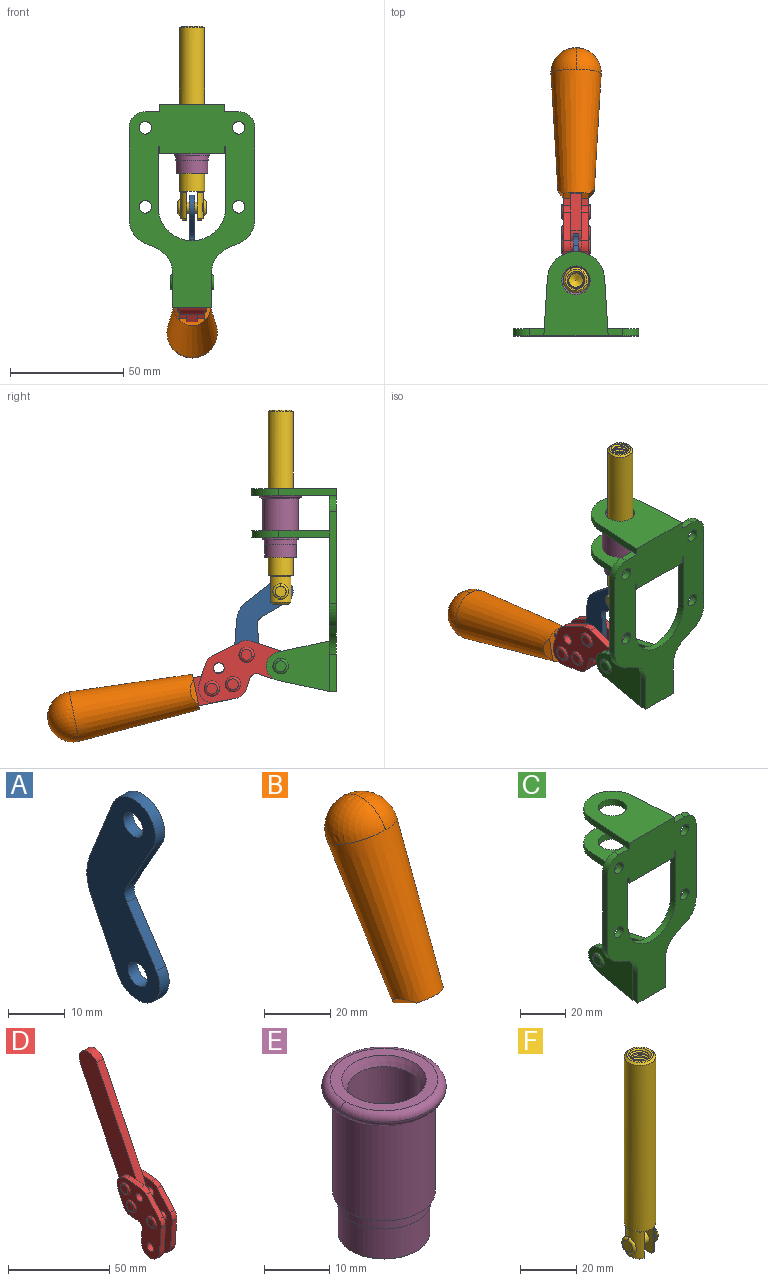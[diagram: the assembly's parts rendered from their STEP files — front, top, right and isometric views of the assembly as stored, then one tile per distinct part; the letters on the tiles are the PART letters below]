
ASSEMBLY  parts=6 mates=6
PART A: 12 faces, bbox 2.3x18.2x42.8 mm
  f0: cylinder r=2.4mm len=4.8mm, axis (1,0,0), area 34.9mm2, adj f4,f11
  f1: cylinder r=10.41mm len=8.47mm, axis (1,0,0), area 20.2mm2, adj f4,f9,f10,f11
  f2: cylinder r=3.05mm len=3.16mm, axis (1,0,0), area 7.7mm2, adj f4,f6,f7,f11
  f3: cylinder r=2.4mm len=4.8mm, axis (1,0,0), area 34.9mm2, adj f4,f11
  f4: plane 42.81x18.23mm, normal (-1,0,0), area 414.1mm2, adj f0,f1,f2,f3,f5,f6,f7,f8
  f5: cylinder r=5.54mm len=10.67mm, axis (1,0,0), area 41.8mm2, adj f4,f6,f10,f11
  f6: plane 11.66x6.53mm, normal (0,-0.87,-0.49), area 30.9mm2, adj f2,f4,f5,f11
  f7: plane 11.17x7.33mm, normal (0,-0.84,0.55), area 30.9mm2, adj f2,f4,f8,f11
  f8: cylinder r=5.54mm len=10.51mm, axis (1,0,0), area 41.8mm2, adj f4,f7,f9,f11
  f9: plane 13.67x6.67mm, normal (0,0.9,-0.44), area 35.1mm2, adj f1,f4,f8,f11
  f10: plane 14.1x5.7mm, normal (0,0.93,0.37), area 35.1mm2, adj f1,f4,f5,f11
  f11: plane 42.81x18.23mm, normal (1,0,0), area 414.1mm2, adj f0,f1,f2,f3,f5,f6,f7,f8
PART B: 11 faces, bbox 22.3x42.6x64.5 mm
  f0: sphere r=11.13mm, area 411.4mm2, adj f1,f8
  f1: cone r=11.11mm half-angle=3.3deg, axis (0,0.44,0.9), area 3251.8mm2, adj f0,f7,f8,f9,f10
  f2: cylinder r=6.16mm len=11.7mm, axis (1,0,0), area 89.5mm2, adj f3,f4,f5,f6
  f3: plane 60.23x36.75mm, normal (-1,0,0), area 763.6mm2, adj f2,f4,f6,f10
  f4: plane 51.37x25.05mm, normal (0,0.9,-0.44), area 264.2mm2, adj f2,f3,f5,f10
  f5: plane 60.23x36.75mm, normal (1,0,0), area 763.6mm2, adj f2,f4,f6,f10
  f6: plane 51.37x25.05mm, normal (0,-0.9,0.44), area 264.2mm2, adj f2,f3,f5,f10
  f7: plane 9.95x5.95mm, normal (0.71,-0.31,-0.64), area 25.8mm2, adj f1,f10
  f8: sphere r=11.13mm, area 411.4mm2, adj f0,f1
  f9: plane 9.95x5.95mm, normal (-0.71,-0.31,-0.64), area 25.8mm2, adj f1,f10
  f10: plane 14.27x11.38mm, normal (0,-0.44,-0.9), area 106.7mm2, adj f1,f3,f4,f5,f6,f7,f9
PART C: 55 faces, bbox 55.7x37.4x89.8 mm
  f0: torus R=2.41mm, axis (-1,0,0), area 15mm2, adj f11,f15,f25
  f1: torus R=2.41mm, axis (-1,0,0), area 15mm2, adj f10,f12,f22
  f2: cylinder r=2.78mm len=5.56mm, axis (0,-1,0), area 54.2mm2, adj f30,f54
  f3: cylinder r=14.99mm len=29.97mm, axis (0,-1,0), area 145.9mm2, adj f30,f49,f53,f54
  f4: cylinder r=2.78mm len=5.56mm, axis (0,-1,0), area 54.2mm2, adj f30,f54
  f5: cylinder r=2.78mm len=5.56mm, axis (0,-1,0), area 54.2mm2, adj f30,f54
  f6: cylinder r=2.78mm len=5.56mm, axis (0,-1,0), area 54.2mm2, adj f30,f54
  f7: cylinder r=6.35mm len=12.7mm, axis (0,0,1), area 123.6mm2, adj f27,f51
  f8: cylinder r=6.35mm len=12.7mm, axis (0,0,-1), area 124.7mm2, adj f21,f35
  f9: cylinder r=2.41mm len=11.18mm, axis (-1,0,0), area 169.4mm2, adj f16,f19
  f10: plane 4.83x4.83mm, normal (1,0,0), area 18.3mm2, adj f1,f12
  f11: plane 4.83x4.83mm, normal (-1,0,0), area 18.3mm2, adj f0,f15
  f12: torus R=2.41mm, axis (-1,0,0), area 15mm2, adj f1,f10,f22
  f13: cylinder r=6.35mm len=12.41mm, axis (1,0,0), area 53.4mm2, adj f18,f19,f22,f23
  f14: cylinder r=6.35mm len=12.41mm, axis (-1,0,0), area 53.4mm2, adj f16,f17,f24,f25
  f15: torus R=2.41mm, axis (-1,0,0), area 15mm2, adj f0,f11,f25
  f16: plane 27.86x22.35mm, normal (1,0,0), area 425.4mm2, adj f9,f14,f17,f24,f30
  f17: plane 22.86x4.97mm, normal (0,0.21,0.98), area 72.5mm2, adj f14,f16,f25,f30
  f18: plane 22.86x4.97mm, normal (0,0.21,0.98), area 72.5mm2, adj f13,f19,f22,f30
  f19: plane 27.86x22.35mm, normal (-1,0,0), area 425.4mm2, adj f9,f13,f18,f23,f30
  f20: cylinder r=12.7mm len=25.35mm, axis (0,0,-1), area 119.8mm2, adj f21,f34,f35,f36
  f21: plane 34.21x28.07mm, normal (0,0,-1), area 702.4mm2, adj f8,f20,f30,f34,f36
  f22: plane 27.96x22.45mm, normal (1,0,0), area 407.2mm2, adj f1,f12,f13,f18,f23,f30,f42,f43
  f23: plane 22.86x4.97mm, normal (0,0.21,-0.98), area 72.5mm2, adj f13,f19,f22,f44
  f24: plane 22.86x4.97mm, normal (0,0.21,-0.98), area 72.5mm2, adj f14,f16,f25,f44
  f25: plane 27.86x22.35mm, normal (-1,0,0), area 407.1mm2, adj f0,f14,f15,f17,f24,f30,f45,f46
  f26: plane 3.1x0.95mm, normal (0,0,-1), area 2.7mm2, adj f30,f49,f50,f54
  f27: plane 34.21x28.07mm, normal (0,0,1), area 702.4mm2, adj f7,f28,f30,f50,f52
  f28: cylinder r=12.7mm len=25.35mm, axis (0,0,1), area 118.8mm2, adj f27,f50,f51,f52
  f29: plane 3.1x0.95mm, normal (0,0,-1), area 2.7mm2, adj f30,f52,f53,f54
  f30: plane 86.54x55.63mm, normal (0,1,0), area 2362.9mm2, adj f2,f3,f4,f5,f6,f16,f17,f18
  f31: plane 40.56x3.1mm, normal (-1,0,0), area 125.7mm2, adj f30,f32,f48,f54
  f32: cylinder r=7.11mm len=7.11mm, axis (0,-1,0), area 34.6mm2, adj f30,f31,f33,f54
  f33: plane 6.67x3.1mm, normal (0,0,1), area 20.4mm2, adj f30,f32,f34,f54
  f34: plane 25.39x3.13mm, normal (-1,0.06,0), area 79.5mm2, adj f20,f21,f33,f35,f54
  f35: plane 37.31x28.45mm, normal (0,0,1), area 789.9mm2, adj f8,f20,f34,f36,f54
  f36: plane 25.39x3.13mm, normal (1,0.06,0), area 79.5mm2, adj f20,f21,f35,f37,f54
  f37: plane 6.67x3.1mm, normal (0,0,1), area 20.4mm2, adj f30,f36,f38,f54
  f38: cylinder r=7.11mm len=7.11mm, axis (0,-1,0), area 34.6mm2, adj f30,f37,f39,f54
  f39: plane 40.56x3.1mm, normal (1,0,0), area 125.7mm2, adj f30,f38,f40,f54
  f40: cylinder r=11.18mm len=10.16mm, axis (0,-1,0), area 39.5mm2, adj f30,f39,f41,f54
  f41: plane 6.09x3.1mm, normal (0.42,0,-0.91), area 20.8mm2, adj f30,f40,f42,f54
  f42: cylinder r=11.18mm len=9.41mm, axis (0,-1,0), area 37.2mm2, adj f22,f30,f41,f43,f54
  f43: plane 16.5x3.1mm, normal (1,0,0), area 51.1mm2, adj f22,f42,f44,f54
  f44: plane 17.37x3.1mm, normal (0,0,-1), area 53.8mm2, adj f23,f24,f30,f43,f45,f54
  f45: plane 16.5x3.1mm, normal (-1,0,0), area 51.1mm2, adj f25,f44,f46,f54
  f46: cylinder r=11.18mm len=9.41mm, axis (0,-1,0), area 37.2mm2, adj f25,f30,f45,f47,f54
  f47: plane 6.09x3.1mm, normal (-0.42,0,-0.91), area 20.8mm2, adj f30,f46,f48,f54
  f48: cylinder r=11.18mm len=10.16mm, axis (0,-1,0), area 39.5mm2, adj f30,f31,f47,f54
  f49: plane 26.54x3.1mm, normal (-1,0,0), area 82.3mm2, adj f3,f26,f30,f54
  f50: plane 25.39x3.1mm, normal (1,0.06,0), area 78.8mm2, adj f26,f27,f28,f51,f54
  f51: plane 37.31x28.45mm, normal (0,0,-1), area 789.9mm2, adj f7,f28,f50,f52,f54
  f52: plane 25.39x3.1mm, normal (-1,0.06,0), area 78.8mm2, adj f27,f28,f29,f51,f54
  f53: plane 26.54x3.1mm, normal (1,0,0), area 82.3mm2, adj f3,f29,f30,f54
  f54: plane 89.66x55.63mm, normal (0,-1,0), area 2678.5mm2, adj f2,f3,f4,f5,f6,f26,f29,f31
PART D: 59 faces, bbox 12.9x60.2x99.6 mm
  f0: torus R=2.39mm, axis (-1,0,0), area 14.9mm2, adj f20,f43,f51
  f1: torus R=2.39mm, axis (-1,0,0), area 14.9mm2, adj f19,f42,f51
  f2: torus R=2.39mm, axis (-1,0,0), area 14.9mm2, adj f18,f35,f51
  f3: torus R=2.39mm, axis (-1,0,0), area 14.9mm2, adj f14,f17,f23
  f4: torus R=2.39mm, axis (-1,0,0), area 14.9mm2, adj f13,f16,f23
  f5: torus R=2.39mm, axis (-1,0,0), area 14.9mm2, adj f12,f15,f23
  f6: cylinder r=2.39mm len=4.78mm, axis (1,0,0), area 46.5mm2, adj f48,f50,f51
  f7: cylinder r=2.39mm len=4.78mm, axis (1,0,0), area 46.5mm2, adj f50,f51
  f8: cylinder r=6.35mm len=12.68mm, axis (1,0,0), area 61.8mm2, adj f38,f39,f50,f51
  f9: cylinder r=2.39mm len=4.78mm, axis (-1,0,0), area 70.5mm2, adj f46,f50
  f10: cylinder r=2.39mm len=4.78mm, axis (-1,0,0), area 46.5mm2, adj f23,f45,f46
  f11: cylinder r=2.39mm len=4.78mm, axis (-1,0,0), area 46.5mm2, adj f23,f46
  f12: plane 4.78x4.78mm, normal (1,0,0), area 17.9mm2, adj f5,f15
  f13: plane 4.78x4.78mm, normal (1,0,0), area 17.9mm2, adj f4,f16
  f14: plane 4.78x4.78mm, normal (1,0,0), area 17.9mm2, adj f3,f17
  f15: torus R=2.39mm, axis (-1,0,0), area 14.9mm2, adj f5,f12,f23
  f16: torus R=2.39mm, axis (-1,0,0), area 14.9mm2, adj f4,f13,f23
  f17: torus R=2.39mm, axis (-1,0,0), area 14.9mm2, adj f3,f14,f23
  f18: plane 4.78x4.78mm, normal (-1,0,0), area 17.9mm2, adj f2,f35
  f19: plane 4.78x4.78mm, normal (-1,0,0), area 17.9mm2, adj f1,f42
  f20: plane 4.78x4.78mm, normal (-1,0,0), area 17.9mm2, adj f0,f43
  f21: plane 2.26x0.2mm, normal (1,0,0), area 0.2mm2, adj f31,f44
  f22: plane 2.26x0.2mm, normal (-1,0,0), area 0.2mm2, adj f41,f44
  f23: plane 39.37x30.77mm, normal (1,0,0), area 565.5mm2, adj f3,f4,f5,f10,f11,f15,f16,f17
  f24: cylinder r=6.1mm len=4.15mm, axis (-1,0,0), area 14.7mm2, adj f23,f25,f32,f46
  f25: plane 10.25x9.01mm, normal (0,-0.75,0.66), area 42.3mm2, adj f23,f24,f26,f46
  f26: cylinder r=6.35mm len=4.64mm, axis (-1,0,0), area 15.6mm2, adj f23,f25,f27,f46
  f27: plane 15.84x3.1mm, normal (0,-1,-0.07), area 49.2mm2, adj f23,f26,f28,f46
  f28: cylinder r=6.35mm len=12.68mm, axis (-1,0,0), area 61.8mm2, adj f23,f27,f29,f46
  f29: plane 8.11x3.1mm, normal (0,1,0.07), area 25.2mm2, adj f23,f28,f30,f46
  f30: cylinder r=3.05mm len=3.25mm, axis (-1,0,0), area 14.8mm2, adj f23,f29,f31,f46
  f31: plane 5.99x3.1mm, normal (0,0.07,-1), area 18.6mm2, adj f21,f23,f30,f44,f46
  f32: plane 9.5x3.1mm, normal (0,-0.07,1), area 29.5mm2, adj f23,f24,f33,f46,f47
  f33: cylinder r=6.1mm len=8.63mm, axis (-1,0,0), area 39.1mm2, adj f23,f32,f34,f47
  f34: plane 8.65x3.96mm, normal (0,0.91,-0.42), area 29.5mm2, adj f23,f33,f44,f47
  f35: torus R=2.39mm, axis (-1,0,0), area 14.9mm2, adj f2,f18,f51
  f36: plane 10.25x9.01mm, normal (0,-0.75,0.66), area 42.3mm2, adj f37,f49,f50,f51
  f37: cylinder r=6.35mm len=4.64mm, axis (1,0,0), area 15.6mm2, adj f36,f38,f50,f51
  f38: plane 15.84x3.1mm, normal (0,-1,-0.07), area 49.2mm2, adj f8,f37,f50,f51
  f39: plane 8.11x3.1mm, normal (0,1,0.07), area 25.2mm2, adj f8,f40,f50,f51
  f40: cylinder r=3.05mm len=3.25mm, axis (1,0,0), area 14.8mm2, adj f39,f41,f50,f51
  f41: plane 5.99x3.1mm, normal (0,0.07,-1), area 18.6mm2, adj f22,f40,f44,f50,f51
  f42: torus R=2.39mm, axis (-1,0,0), area 14.9mm2, adj f1,f19,f51
  f43: torus R=2.39mm, axis (-1,0,0), area 14.9mm2, adj f0,f20,f51
  f44: cylinder r=6.35mm len=12.12mm, axis (-1,0,0), area 128.9mm2, adj f21,f22,f23,f31,f34,f41,f46,f47
  f45: plane 2.65x1.35mm, normal (1,0,0), area 1mm2, adj f10,f55
  f46: plane 39.08x20.42mm, normal (-1,0,0), area 412.5mm2, adj f9,f10,f11,f24,f25,f26,f27,f28
  f47: plane 77.62x39.82mm, normal (1,0,0), area 850mm2, adj f32,f33,f34,f44,f53,f54,f55
  f48: plane 2.65x1.35mm, normal (-1,0,0), area 1mm2, adj f6,f55
  f49: cylinder r=6.1mm len=4.15mm, axis (1,0,0), area 14.7mm2, adj f36,f50,f51,f56
  f50: plane 39.08x20.42mm, normal (1,0,0), area 412.5mm2, adj f6,f7,f8,f9,f36,f37,f38,f39
  f51: plane 39.37x30.77mm, normal (-1,0,0), area 565.5mm2, adj f0,f1,f2,f6,f7,f8,f35,f36
  f52: plane 8.65x3.96mm, normal (0,0.91,-0.42), area 29.5mm2, adj f44,f51,f57,f58
  f53: plane 68.49x33.4mm, normal (0,0.9,-0.44), area 358.1mm2, adj f44,f47,f54,f58
  f54: cylinder r=6.35mm len=12.06mm, axis (1,0,0), area 93.7mm2, adj f47,f53,f55,f58
  f55: plane 68.49x33.4mm, normal (0,-0.9,0.44), area 358.1mm2, adj f44,f45,f46,f47,f48,f50,f54,f58
  f56: plane 9.5x3.1mm, normal (0,-0.07,1), area 29.5mm2, adj f49,f50,f51,f57,f58
  f57: cylinder r=6.1mm len=8.63mm, axis (1,0,0), area 39.1mm2, adj f51,f52,f56,f58
  f58: plane 77.62x39.82mm, normal (-1,0,0), area 850mm2, adj f44,f52,f53,f54,f55,f56,f57
PART E: 15 faces, bbox 20.6x20.6x28.7 mm
  f0: torus R=8.26mm, axis (0,0,1), area 56.8mm2, adj f1,f10,f12
  f1: torus R=8.26mm, axis (0,0,1), area 56.8mm2, adj f0,f6,f13
  f2: cylinder r=5.59mm len=25.91mm, axis (0,0,1), area 909.6mm2, adj f3,f4
  f3: cone r=6.86mm half-angle=45deg, axis (0,0,-1), area 70.2mm2, adj f2,f14
  f4: cone r=6.47mm half-angle=30deg, axis (0,0,1), area 66.7mm2, adj f2,f13
  f5: cylinder r=7.04mm len=14.07mm, axis (0,0,1), area 252.6mm2, adj f11,f14
  f6: torus R=8.26mm, axis (0,0,1), area 56.8mm2, adj f1,f12,f13
  f7: cylinder r=7.16mm len=14.33mm, axis (0,0,1), area 91.5mm2, adj f9,f11
  f8: cylinder r=7.86mm len=18.42mm, axis (0,0,1), area 909.6mm2, adj f9,f10
  f9: plane 15.72x15.72mm, normal (0,0,-1), area 33mm2, adj f7,f8
  f10: plane 16.51x16.51mm, normal (0,0,-1), area 19.9mm2, adj f0,f8,f12
  f11: plane 14.33x14.33mm, normal (0,0,-1), area 5.7mm2, adj f5,f7
  f12: torus R=8.26mm, axis (0,0,1), area 56.8mm2, adj f0,f6,f10
  f13: plane 16.51x16.51mm, normal (0,0,1), area 82.7mm2, adj f1,f4,f6
  f14: plane 14.07x14.07mm, normal (0,0,-1), area 7.8mm2, adj f3,f5
PART F: 48 faces, bbox 12.6x11.1x86.1 mm
  f0: torus R=2.41mm, axis (-1,0,0), area 15mm2, adj f30,f32,f34
  f1: torus R=2.41mm, axis (-1,0,0), area 15mm2, adj f29,f31,f33
  f2: cylinder r=5.54mm len=72.39mm, axis (0,0,1), area 2518.5mm2, adj f3,f4,f42,f43
  f3: cone r=5.54mm half-angle=45deg, axis (0,0,1), area 7.6mm2, adj f2,f5,f41
  f4: cone r=5.54mm half-angle=45deg, axis (0,0,-1), area 34.9mm2, adj f2,f39
  f5: cylinder r=5.08mm len=11.48mm, axis (0,0,1), area 108.3mm2, adj f3,f7,f8,f41
  f6: cylinder r=2.41mm len=4.83mm, axis (-1,0,0), area 71.2mm2, adj f40,f41
  f7: cylinder r=2.41mm len=4.83mm, axis (-1,0,0), area 7.6mm2, adj f5,f34
  f8: cone r=5.08mm half-angle=45deg, axis (0,0,1), area 10.6mm2, adj f5,f37,f41
  f9: cone r=3.98mm half-angle=45deg, axis (0,0,1), area 17.6mm2, adj f27,f39,f45,f46,f47
  f10: cylinder r=2.41mm len=4.83mm, axis (-1,0,0), area 7.6mm2, adj f33,f38
  f11: cylinder r=3.2mm len=6.4mm, axis (0,0,1), area 78.4mm2, adj f12,f28,f44,f45,f47
  f12: cylinder r=3.2mm len=6.4mm, axis (0,0,1), area 10.5mm2, adj f11,f13,f45,f47
  f13: cylinder r=3.2mm len=6.4mm, axis (0,0,1), area 10.5mm2, adj f12,f14,f45,f47
  f14: cylinder r=3.2mm len=6.4mm, axis (0,0,1), area 10.5mm2, adj f13,f15,f45,f47
  f15: cylinder r=3.2mm len=6.4mm, axis (0,0,1), area 10.5mm2, adj f14,f16,f45,f47
  f16: cylinder r=3.2mm len=6.4mm, axis (0,0,1), area 10.5mm2, adj f15,f17,f45,f47
  f17: cylinder r=3.2mm len=6.4mm, axis (0,0,1), area 10.5mm2, adj f16,f18,f45,f47
  f18: cylinder r=3.2mm len=6.4mm, axis (0,0,1), area 10.5mm2, adj f17,f19,f45,f47
  f19: cylinder r=3.2mm len=6.4mm, axis (0,0,1), area 10.5mm2, adj f18,f20,f45,f47
  f20: cylinder r=3.2mm len=6.4mm, axis (0,0,1), area 10.5mm2, adj f19,f21,f45,f47
  f21: cylinder r=3.2mm len=6.4mm, axis (0,0,1), area 10.5mm2, adj f20,f22,f45,f47
  f22: cylinder r=3.2mm len=6.4mm, axis (0,0,1), area 10.5mm2, adj f21,f23,f45,f47
  f23: cylinder r=3.2mm len=6.4mm, axis (0,0,1), area 10.5mm2, adj f22,f24,f45,f47
  f24: cylinder r=3.2mm len=6.4mm, axis (0,0,1), area 10.5mm2, adj f23,f25,f45,f47
  f25: cylinder r=3.2mm len=6.4mm, axis (0,0,1), area 10.5mm2, adj f24,f26,f45,f47
  f26: cylinder r=3.2mm len=6.4mm, axis (0,0,1), area 10.5mm2, adj f25,f27,f45,f47
  f27: cylinder r=3.2mm len=6.4mm, axis (0,0,1), area 7.4mm2, adj f9,f26,f45,f47
  f28: cone r=3.2mm half-angle=60deg, axis (0,0,1), area 37.2mm2, adj f11
  f29: plane 4.83x4.83mm, normal (-1,0,0), area 18.3mm2, adj f1,f31
  f30: plane 4.83x4.83mm, normal (1,0,0), area 18.3mm2, adj f0,f32
  f31: torus R=2.41mm, axis (-1,0,0), area 15mm2, adj f1,f29,f33
  f32: torus R=2.41mm, axis (-1,0,0), area 15mm2, adj f0,f30,f34
  f33: plane 6.83x6.83mm, normal (1,0,0), area 18.3mm2, adj f1,f10,f31
  f34: plane 6.83x6.83mm, normal (-1,0,0), area 18.3mm2, adj f0,f7,f32
  f35: cone r=5.08mm half-angle=45deg, axis (0,0,1), area 10.6mm2, adj f36,f38,f40
  f36: plane 7.25x1.97mm, normal (0,0,-1), area 10mm2, adj f35,f40
  f37: plane 7.25x1.97mm, normal (0,0,-1), area 10mm2, adj f8,f41
  f38: cylinder r=5.08mm len=11.48mm, axis (0,0,1), area 108.3mm2, adj f10,f35,f40,f42
  f39: plane 9.55x9.55mm, normal (0,0,1), area 22mm2, adj f4,f9
  f40: plane 12.76x10.09mm, normal (1,0,0), area 95.7mm2, adj f6,f35,f36,f38,f42,f43
  f41: plane 12.76x10.09mm, normal (-1,0,0), area 95.7mm2, adj f3,f5,f6,f8,f37,f43
  f42: cone r=5.54mm half-angle=45deg, axis (0,0,1), area 7.6mm2, adj f2,f38,f40
  f43: plane 11.07x4.7mm, normal (0,0,-1), area 50.4mm2, adj f2,f40,f41
  f44: plane 0.89x0.62mm, normal (-1,0,0), area 0.3mm2, adj f11,f45,f46,f47
  f45: bspline ~24.8x7.63mm, area 266.6mm2, adj f9,f11,f12,f13,f14,f15,f16,f17
  f46: bspline ~24.87x7.63mm, area 73.6mm2, adj f9,f44,f45,f47
  f47: bspline ~24.98x7.63mm, area 272.5mm2, adj f9,f11,f12,f13,f14,f15,f16,f17
PLACE A rot(axis=(1,0,0),30.3deg) t=(-9.07,-32.41,-25.99)mm
PLACE B rot(axis=(-1,0,0),75.5deg) t=(-9.03,3.62,-0.89)mm
PLACE C t=(-9.07,-43.58,-1.12)mm fixed
PLACE D rot(axis=(-1,0,0),75.5deg) t=(-9.07,5.93,-1.33)mm
PLACE E t=(-9.07,-43.58,-5.26)mm
PLACE F rot(axis=(0,0,1),180deg) t=(-9.07,5.65,-15.68)mm
MATE revolute A.f3 <-> D.f4  axis (1,0,0) through (-9.07,-3.91,-28.17)mm
MATE fastened B.f3 <-> D.f47  axis (-1,0,0) through (-6.72,48.85,-50.72)mm
MATE slider F.f2 <-> E.f2  axis (0,0,1) through (-9.07,-18.96,-5.04)mm
MATE fastened E.f2 <-> C.f7  axis (0,0,1) through (-9.07,-18.96,42.15)mm
MATE revolute A.f5 <-> F.f6  axis (1,0,0) through (-9.07,-18.96,-0.21)mm
MATE revolute D.f7 <-> C.f0  axis (-1,0,0) through (-9.07,-18.96,-33.21)mm
